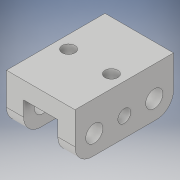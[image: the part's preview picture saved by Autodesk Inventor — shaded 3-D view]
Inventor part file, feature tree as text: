
AUTODESK INVENTOR PART (.ipt)
format: ipt  version: 2019 (Build 230136000, 136)  size: 168,960 bytes
history: native  units: mm
features: sketch x4, hole x3, extrude x2, fillet x1
ambient origin geometry x8: Origin, YZ Plane, XZ Plane, XY Plane, X Axis, Y Axis, Z Axis, Center Point
bodies: Solid1 (feature_tree)
feature tree (10):
  extrude  "Extrusion1"  Depth=80.0mm
  extrude  "Extrusion11"  Depth=20.0mm
  sketch  "Sketch13"  dims[d57=115.0mm d58=37.5mm d59=0.0mm]
  hole  "Hole2"  [1 undecoded]
  hole  "Hole3"  [1 undecoded]
  hole  "Hole6"  [1 undecoded]
  fillet  "Fillet19"  Radius=20.0mm
  sketch  "Sketch1"  dims[d0=115.0mm d1=80.0mm]
  sketch  "Sketch12"  dims[d2=20.0mm d3=0.0mm d56=20.0mm]
  sketch  "Sketch19"  dims[d63=20.0mm d64=6.0mm d65=4.0mm d66=2.0mm d67=90.0deg d68=8.0mm d69=20.594885mm d70=15.0mm d71=6.0mm d72=4.0mm d73=2.0mm d74=90.0deg d75=8.0mm d76=20.594885mm d111=25.0mm d112=25.0mm d113=15.0mm d114=6.0mm d115=4.0mm d116=2.0mm d117=90.0deg d118=15.0mm d119=0.0mm d120=20.0mm d129=35.0mm d130=35.0mm d131=15.0mm d12=1.0mm d13=1.0mm d14=1.0mm d15=0.15mm d16=0.25mm d17=0.375mm d18=14.3117mm d19=0.75mm d20=20.594885mm d21=0.0625mm d22=0.75mm d23=0.375mm]
note: 3 required parameter values undecoded (feature->parameter linkage not recoverable at this tier; creation-order binding heuristic only, values carry confidence <= 0.55)
